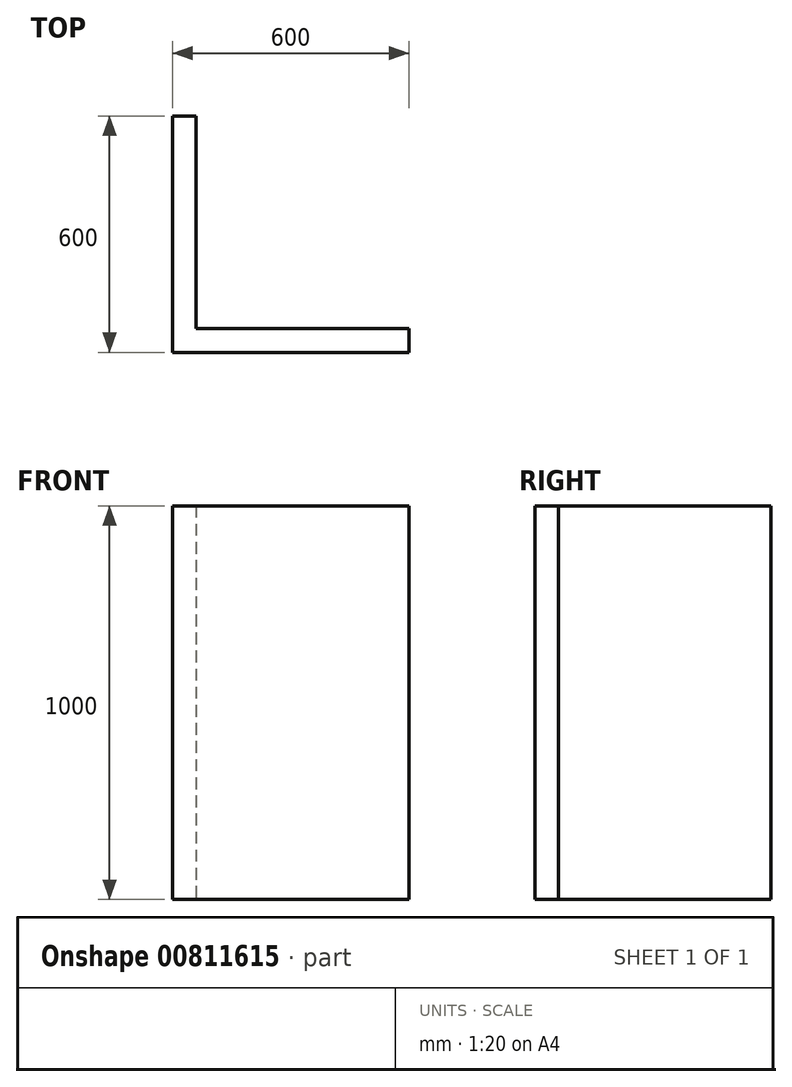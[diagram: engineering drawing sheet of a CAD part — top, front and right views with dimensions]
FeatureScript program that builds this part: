
annotation { "Feature Type Name" : "Feature", "Feature Type Description" : "" }
export const myFeature = defineFeature(function(context is Context, id is Id, definition is map)
    precondition{}
    {
        {
            var Q0;
            Q0=qCreatedBy(makeId("Top.planeOp"),FACE);
            var sketch = newSketch(context, id + "F0", { "sketchPlane" : qUnion([Q0])});
            skLineSegment(sketch, "E0.top", {"start": v(-4392.96, -2296.23) * mm, "end": v(-3792.96, -2296.23) * mm});
            skLineSegment(sketch, "E0.left", {"start": v(-4392.96, -1696.23) * mm, "end": v(-4392.96, -2296.23) * mm});
            skLineSegment(sketch, "E1", {"start": v(-3792.96, -2296.23) * mm, "end": v(-3792.96, -2236.23) * mm});
            skLineSegment(sketch, "E2", {"start": v(-3792.96, -2236.23) * mm, "end": v(-4332.96, -2236.23) * mm});
            skLineSegment(sketch, "E3", {"start": v(-4332.96, -2236.23) * mm, "end": v(-4332.96, -1696.23) * mm});
            skLineSegment(sketch, "E4", {"start": v(-4332.96, -1696.23) * mm, "end": v(-4392.96, -1696.23) * mm});
            skSolve(sketch);
        }
        {
            var Q0;
            Q0=qSketchRegion(id+"F0",true);
            extrude(context, id + "F1", {"entities" : qUnion([Q0]), "depth" : 1000 * mm, "offsetDistance" : 25 * mm});
        }
    });
